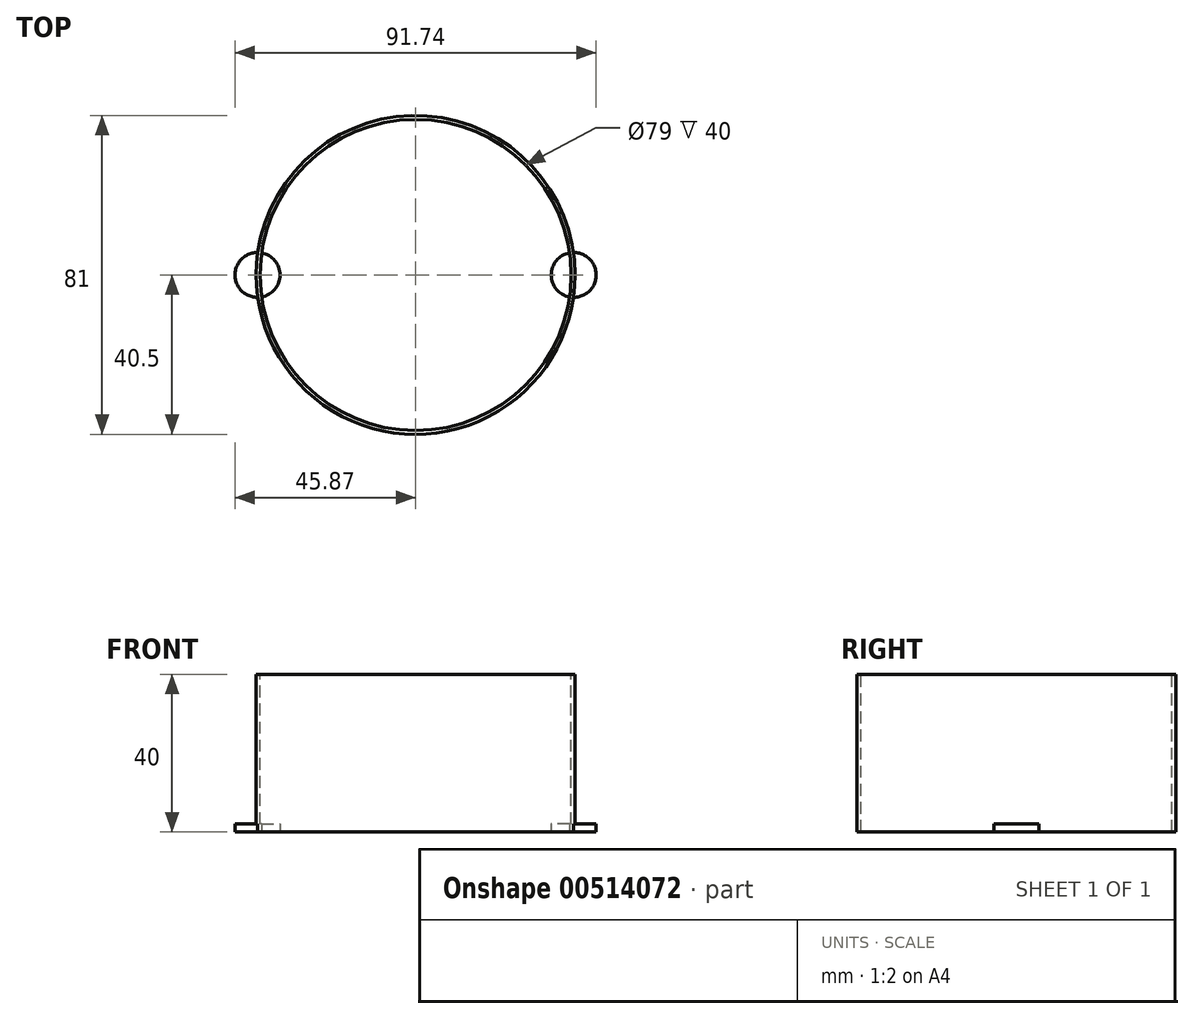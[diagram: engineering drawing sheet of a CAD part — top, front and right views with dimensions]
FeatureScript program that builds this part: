
annotation { "Feature Type Name" : "Feature", "Feature Type Description" : "" }
export const myFeature = defineFeature(function(context is Context, id is Id, definition is map)
    precondition{}
    {
        {
            var Q0;
            Q0=qCreatedBy(makeId("Top.planeOp"),FACE);
            var sketch = newSketch(context, id + "F0", { "sketchPlane" : qUnion([Q0])});
            skCircle(sketch, "E0", {"center": v(0, 0) * mm, "radius": 40.5 * mm});
            skSolve(sketch);
        }
        {
            var Q0;
            Q0 = qSketchRegion(id + "F0", true);
            extrude(context, id + "F1", {"entities" : qUnion([Q0]), "depth" : 40 * mm});
        }
        {
            var Q0;
            Q0=makeQuery(id+"F1.opExtrude","CAP_FACE",FACE,{"disambiguationData":[OSD([sQuery(id+"F0.wireOp",EDGE,"E0")])],"isStart":false});
            var sketch = newSketch(context, id + "F2", { "sketchPlane" : qUnion([Q0])});
            skCircle(sketch, "E1", {"center": v(0, 0) * mm, "radius": 39.5 * mm});
            skSolve(sketch);
        }
        {
            var Q0;
            Q0=makeQuery(id+"F2.imprint","IMPRINT",FACE,{"disambiguationData":[TD([[makeQuery(id+"F2.imprint","IMPRINT",EDGE,{"derivedFrom":sQuery(id+"F2.wireOp",EDGE,"E1")}),1.0]])]});
            extrude(context, id + "F3", {"entities" : qUnion([Q0]), "operationType" : NewBodyOperationType.REMOVE, "oppositeDirection" : true, "depth" : 42 * mm});
        }
        {
            var Q0;
            Q0=qCreatedBy(makeId("Top.planeOp"),FACE);
            var sketch = newSketch(context, id + "F4", { "sketchPlane" : qUnion([Q0])});
            skCircle(sketch, "E2", {"center": v(-40.17, 0) * mm, "radius": 5.7 * mm});
            skCircle(sketch, "E3.MirrorC", {"center": v(40.17, 0) * mm, "radius": 5.7 * mm});
            skSolve(sketch);
        }
        {
            var Q0;
            Q0 = qSketchRegion(id + "F4", true);
            extrude(context, id + "F5", {"entities" : qUnion([Q0]), "operationType" : NewBodyOperationType.ADD, "depth" : 2 * mm});
        }
    });
